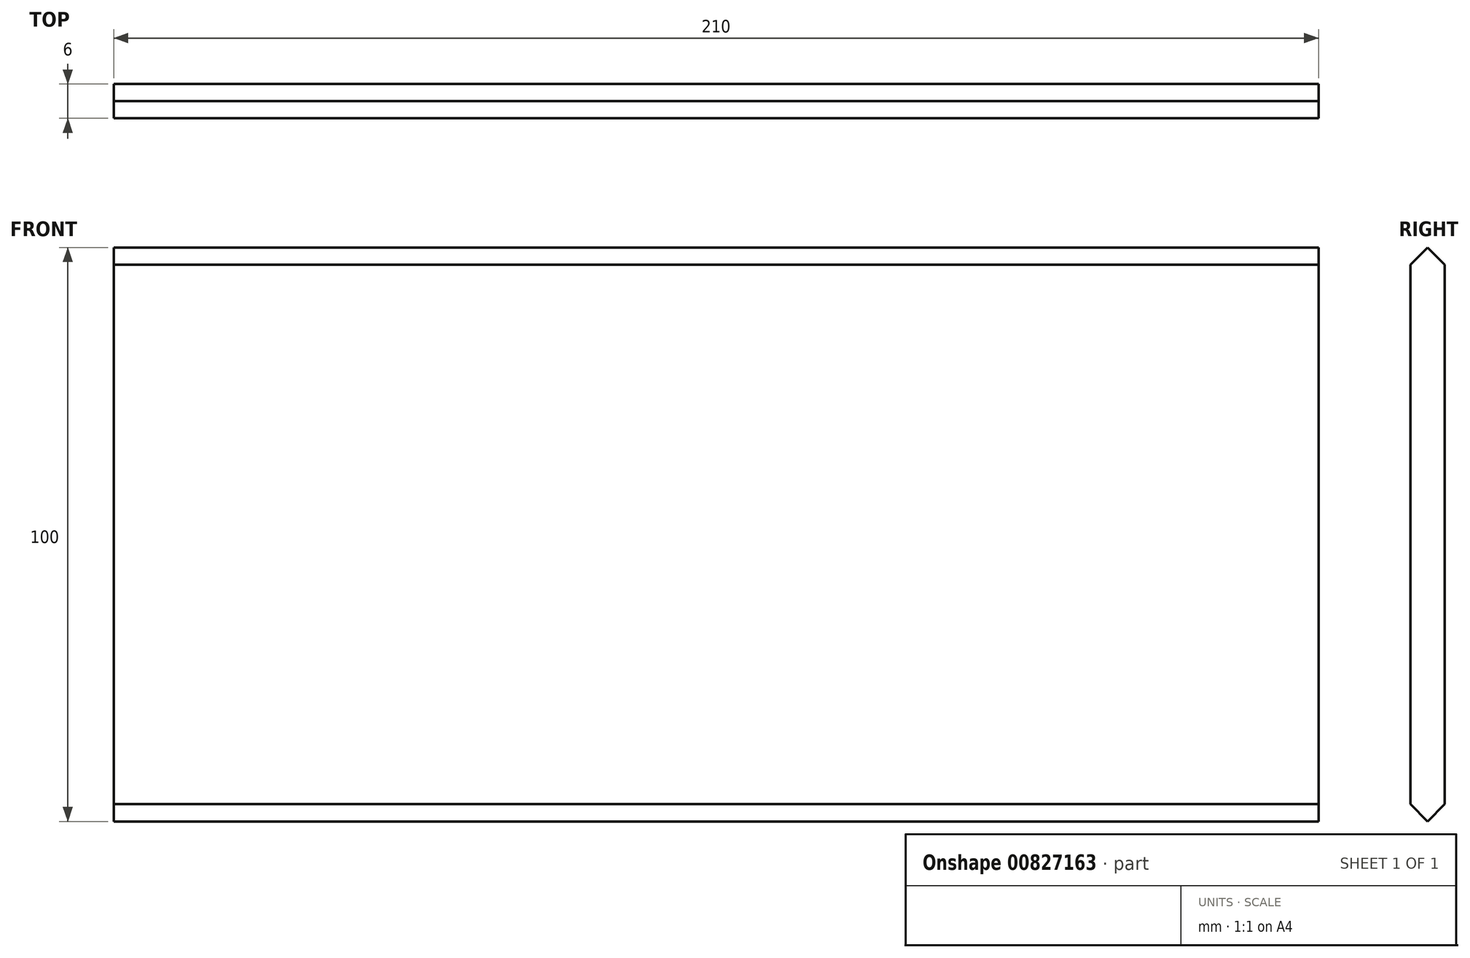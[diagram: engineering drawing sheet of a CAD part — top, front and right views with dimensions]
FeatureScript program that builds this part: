
annotation { "Feature Type Name" : "Feature", "Feature Type Description" : "" }
export const myFeature = defineFeature(function(context is Context, id is Id, definition is map)
    precondition{}
    {
        {
            var Q0;
            Q0=qCreatedBy(makeId("Right.planeOp"),FACE);
            var sketch = newSketch(context, id + "F0", { "sketchPlane" : qUnion([Q0])});
            skLineSegment(sketch, "E0.left", {"start": v(1, 15.5) * mm, "end": v(1, 109.5) * mm});
            skLineSegment(sketch, "E0.right", {"start": v(7, 15.5) * mm, "end": v(7, 109.5) * mm});
            skLineSegment(sketch, "E1", {"start": v(1, 109.5) * mm, "end": v(4, 109.5) * mm, "construction": true});
            skLineSegment(sketch, "E2", {"start": v(1, 109.5) * mm, "end": v(4, 112.5) * mm});
            skLineSegment(sketch, "E3", {"start": v(4, 112.5) * mm, "end": v(7, 109.5) * mm});
            skPoint(sketch, "E4.orphan", {"position": v(1, 112.5) * mm});
            skPoint(sketch, "E5.end.orphan", {"position": v(7, 112.5) * mm});
            skLineSegment(sketch, "E6", {"start": v(1, 15.5) * mm, "end": v(7, 15.5) * mm, "construction": true});
            skLineSegment(sketch, "E7", {"start": v(1, 15.5) * mm, "end": v(4, 12.5) * mm});
            skLineSegment(sketch, "E8", {"start": v(4, 12.5) * mm, "end": v(7, 15.5) * mm});
            skPoint(sketch, "E9.orphan", {"position": v(7, 12.5) * mm});
            skPoint(sketch, "E10.orphan", {"position": v(1, 12.5) * mm});
            skSolve(sketch);
        }
        {
            var Q0;
            Q0=makeQuery(id+"F0.imprint","IMPRINT",FACE,{"disambiguationData":[TD([[makeQuery(id+"F0.imprint","IMPRINT",EDGE,{"derivedFrom":sQuery(id+"F0.wireOp",EDGE,"E0.left")}),-1.0]])]});
            extrude(context, id + "F1", {"entities" : qUnion([Q0]), "depth" : 210 * mm, "offsetDistance" : 25 * mm});
        }
    });
